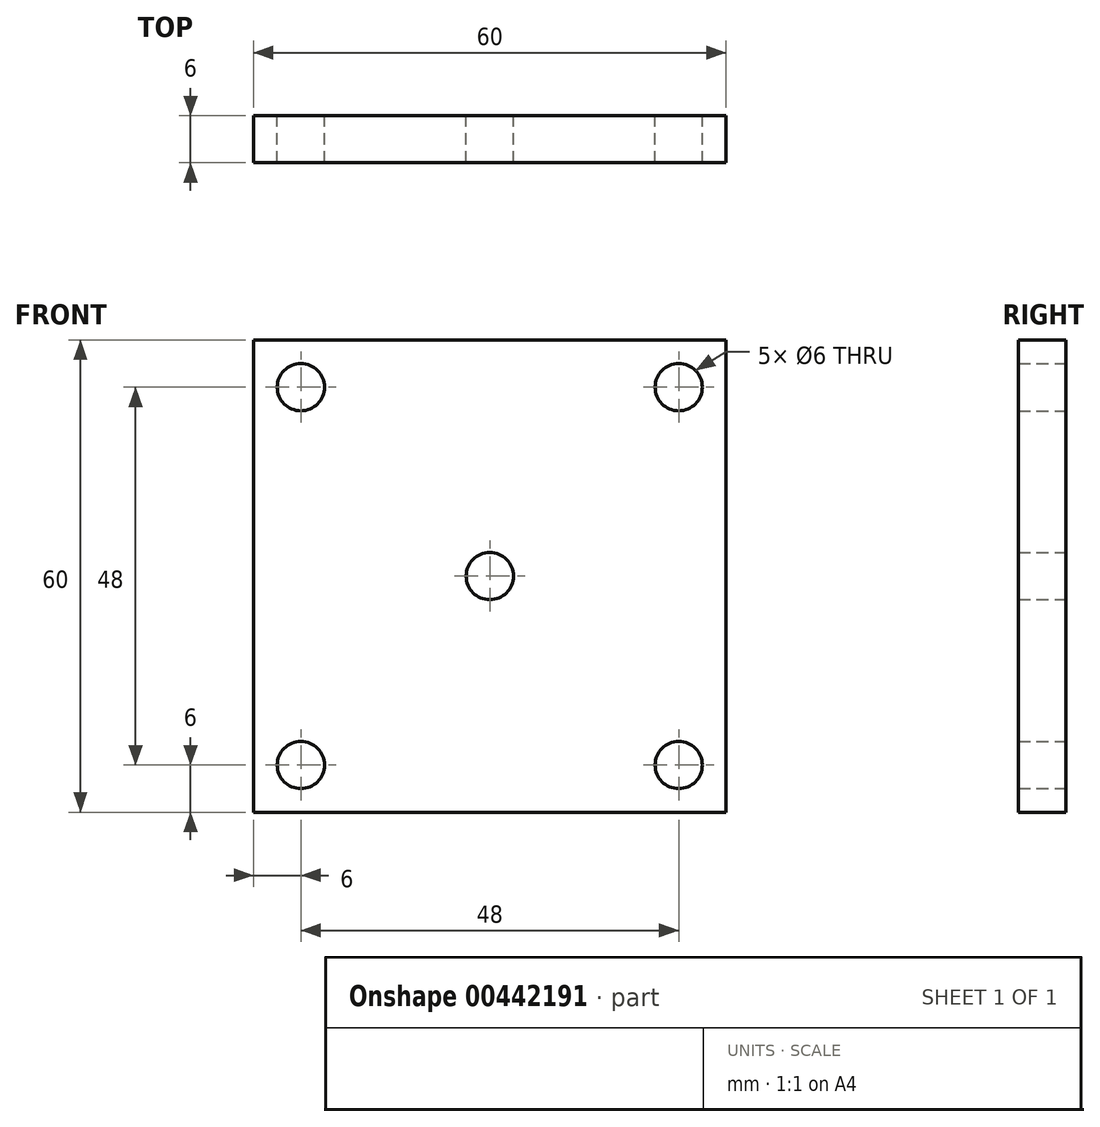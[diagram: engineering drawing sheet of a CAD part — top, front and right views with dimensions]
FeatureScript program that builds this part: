
annotation { "Feature Type Name" : "Feature", "Feature Type Description" : "" }
export const myFeature = defineFeature(function(context is Context, id is Id, definition is map)
    precondition{}
    {
        {
            var Q0;
            Q0=qCreatedBy(makeId("Front.planeOp"),FACE);
            var sketch = newSketch(context, id + "F0", { "sketchPlane" : qUnion([Q0])});
            skLineSegment(sketch, "E0.bottom", {"start": v(30, 30) * mm, "end": v(-30, 30) * mm});
            skLineSegment(sketch, "E0.top", {"start": v(30, -30) * mm, "end": v(-30, -30) * mm});
            skLineSegment(sketch, "E0.left", {"start": v(30, 30) * mm, "end": v(30, -30) * mm});
            skLineSegment(sketch, "E0.right", {"start": v(-30, 30) * mm, "end": v(-30, -30) * mm});
            skPoint(sketch, "E0.middle", {"position": v(0, 0) * mm});
            skCircle(sketch, "E1", {"center": v(-24, 24) * mm, "radius": 3 * mm});
            skCircle(sketch, "E2", {"center": v(24, 24) * mm, "radius": 3 * mm});
            skCircle(sketch, "E3", {"center": v(24, -24) * mm, "radius": 3 * mm});
            skCircle(sketch, "E4", {"center": v(-24, -24) * mm, "radius": 3 * mm});
            skCircle(sketch, "E5", {"center": v(0, 0) * mm, "radius": 3 * mm});
            skSolve(sketch);
        }
        {
            var Q0;
            Q0=makeQuery(id+"F0.imprint","IMPRINT",FACE,{"disambiguationData":[TD([[makeQuery(id+"F0.imprint","IMPRINT",EDGE,{"derivedFrom":sQuery(id+"F0.wireOp",EDGE,"E0.bottom")}),1.0]])]});
            extrude(context, id + "F1", {"entities" : qUnion([Q0]), "depth" : 6 * mm});
        }
    });
